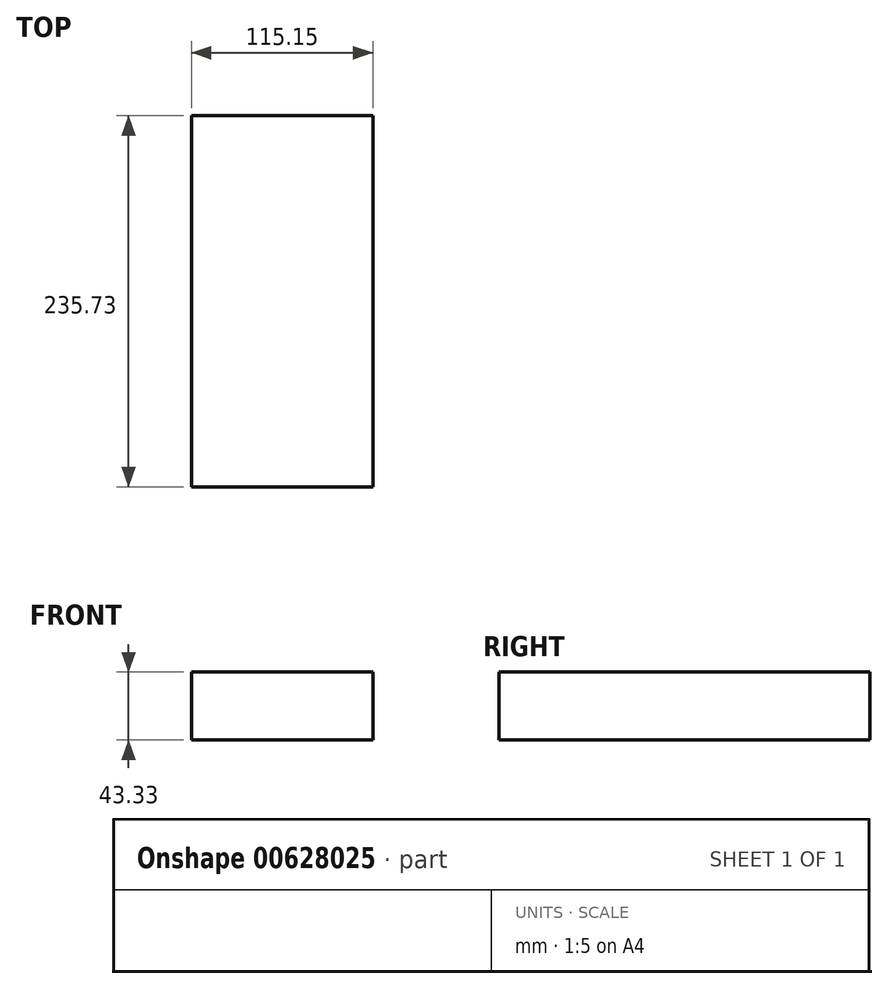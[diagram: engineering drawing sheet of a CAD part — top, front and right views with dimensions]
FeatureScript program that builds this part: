
annotation { "Feature Type Name" : "Feature", "Feature Type Description" : "" }
export const myFeature = defineFeature(function(context is Context, id is Id, definition is map)
    precondition{}
    {
        {
            var Q0;
            Q0=qCreatedBy(makeId("Front.planeOp"),FACE);
            var sketch = newSketch(context, id + "F0", { "sketchPlane" : qUnion([Q0])});
            skLineSegment(sketch, "E0.bottom", {"start": v(0, 0) * mm, "end": v(115.15, 0) * mm});
            skLineSegment(sketch, "E0.top", {"start": v(0, 43.33) * mm, "end": v(115.15, 43.33) * mm});
            skLineSegment(sketch, "E0.left", {"start": v(0, 0) * mm, "end": v(0, 43.33) * mm});
            skLineSegment(sketch, "E0.right", {"start": v(115.15, 0) * mm, "end": v(115.15, 43.33) * mm});
            skSolve(sketch);
        }
        {
            var Q0;
            Q0=makeQuery(id+"F0.imprint","IMPRINT",FACE,{"disambiguationData":[TD([[makeQuery(id+"F0.imprint","IMPRINT",EDGE,{"derivedFrom":sQuery(id+"F0.wireOp",EDGE,"E0.bottom")}),1.0]])]});
            extrude(context, id + "F1", {"entities" : qUnion([Q0]), "depth" : 235.73 * mm, "offsetDistance" : 25.4 * mm});
        }
        {
            var Q0;
            Q0=makeQuery(id+"F1.opExtrude","CAP_FACE",FACE,{"disambiguationData":[OSD([sQuery(id+"F0.wireOp",EDGE,"E0.bottom"),sQuery(id+"F0.wireOp",EDGE,"E0.top"),sQuery(id+"F0.wireOp",EDGE,"E0.left"),sQuery(id+"F0.wireOp",EDGE,"E0.right")])],"isStart":false});
            var sketch = newSketch(context, id + "F2", { "sketchPlane" : qUnion([Q0])});
            skLineSegment(sketch, "E1.bottom", {"start": v(8.4, 43.33) * mm, "end": v(104.15, 43.33) * mm});
            skLineSegment(sketch, "E1.top", {"start": v(8.4, 8.34) * mm, "end": v(104.15, 8.34) * mm});
            skLineSegment(sketch, "E1.left", {"start": v(8.4, 43.33) * mm, "end": v(8.4, 8.34) * mm});
            skLineSegment(sketch, "E1.right", {"start": v(104.15, 43.33) * mm, "end": v(104.15, 8.34) * mm});
            skSolve(sketch);
        }
        {
            var Q0;
            Q0=makeQuery(id+"F2.imprint","IMPRINT",FACE,{"disambiguationData":[TD([[makeQuery(id+"F2.imprint","IMPRINT",EDGE,{"derivedFrom":sQuery(id+"F2.wireOp",EDGE,"E1.bottom")}),-1.0]])]});
            extrude(context, id + "F3", {"entities" : qUnion([Q0]), "operationType" : NewBodyOperationType.ADD, "oppositeDirection" : true, "depth" : 128.97 * mm, "offsetDistance" : 25.4 * mm});
        }
    });
